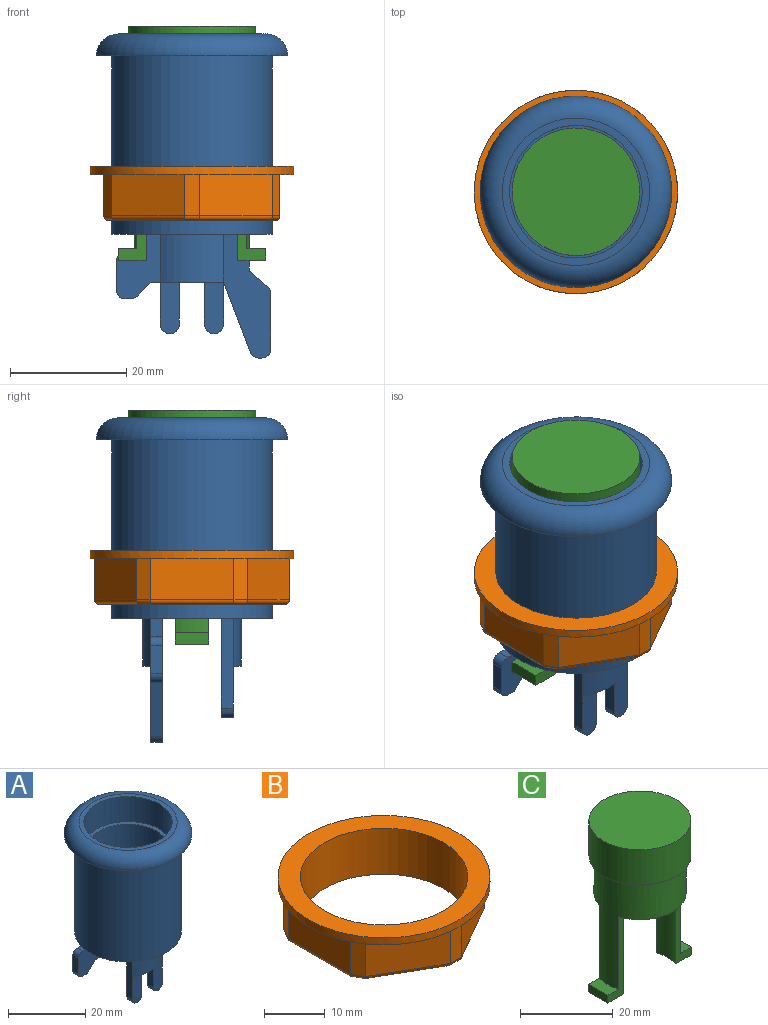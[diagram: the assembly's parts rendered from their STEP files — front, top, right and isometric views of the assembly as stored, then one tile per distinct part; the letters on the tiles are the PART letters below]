
ASSEMBLY  parts=3 mates=2
PART A: 49 faces, bbox 35.7x35.7x55.9 mm
  f0: plane 11.11x7.62mm, normal (0,1,0), area 64.9mm2, adj f1,f29,f30,f31,f37,f38,f39,f42
  f1: plane 27.69x27.69mm, normal (0,0,-1), area 449.5mm2, adj f0,f5,f11,f12,f13,f14,f15,f16
  f2: plane 8.89x3.3mm, normal (0,-1,0), area 28.2mm2, adj f19,f20,f21,f27
  f3: plane 20.57x20.57mm, normal (0,0,1), area 263mm2, adj f10,f11,f12,f13,f14,f15,f16,f17
  f4: plane 25.4x25.4mm, normal (0,0,1), area 96.3mm2, adj f7,f8
  f5: cylinder r=13.84mm len=30.73mm, axis (0,0,1), area 2673.2mm2, adj f1,f6
  f6: plane 33.02x33.02mm, normal (0,0,-1), area 254.3mm2, adj f5,f7
  f7: torus R=12.7mm, axis (0,0,1), area 568.8mm2, adj f4,f6
  f8: cylinder r=11.43mm len=22.86mm, axis (0,0,1), area 570mm2, adj f4,f9
  f9: plane 22.86x22.86mm, normal (0,0,1), area 78mm2, adj f8,f10
  f10: cylinder r=10.29mm len=20.57mm, axis (0,0,1), area 1231.3mm2, adj f3,f9
  f11: plane 7.56x6.48mm, normal (1,0,0), area 48.9mm2, adj f1,f3,f12,f14
  f12: plane 7.56x5mm, normal (0,-1,0), area 37.8mm2, adj f1,f3,f11,f13
  f13: cylinder r=10.03mm len=7.56mm, axis (0,0,-1), area 49.8mm2, adj f1,f3,f12,f14
  f14: plane 7.56x5mm, normal (0,1,0), area 37.8mm2, adj f1,f3,f11,f13
  f15: plane 7.56x6.48mm, normal (-1,0,0), area 48.9mm2, adj f1,f3,f16,f18
  f16: plane 7.56x5mm, normal (0,1,0), area 37.8mm2, adj f1,f3,f15,f17
  f17: cylinder r=10.03mm len=7.56mm, axis (0,0,-1), area 49.8mm2, adj f1,f3,f16,f18
  f18: plane 7.56x5mm, normal (0,-1,0), area 37.8mm2, adj f1,f3,f15,f17
  f19: plane 15.49x2.03mm, normal (-1,0,0), area 31.5mm2, adj f1,f2,f25,f26,f27
  f20: plane 7.24x2.03mm, normal (1,0,0), area 14.7mm2, adj f2,f21,f25,f27
  f21: plane 10.92x3.43mm, normal (0,0,-1), area 19.1mm2, adj f2,f20,f22,f24,f25,f26
  f22: plane 7.24x2.03mm, normal (-1,0,0), area 14.7mm2, adj f21,f24,f25,f28
  f23: plane 15.49x2.03mm, normal (1,0,0), area 31.5mm2, adj f1,f24,f25,f26,f28
  f24: plane 8.89x3.3mm, normal (0,-1,0), area 28.2mm2, adj f21,f22,f23,f28
  f25: plane 17.15x10.92mm, normal (0,1,0), area 146.5mm2, adj f1,f19,f20,f21,f22,f23,f27,f28
  f26: cylinder r=11.37mm len=10.92mm, axis (0,0,1), area 94mm2, adj f1,f19,f21,f23
  f27: cylinder r=1.65mm len=3.3mm, axis (0,1,0), area 10.5mm2, adj f2,f19,f20,f25
  f28: cylinder r=1.65mm len=3.3mm, axis (0,1,0), area 10.5mm2, adj f22,f23,f24,f25
  f29: plane 2.03x1.02mm, normal (0,0,-1), area 2.1mm2, adj f0,f41,f43,f48
  f30: plane 2.41x2.41mm, normal (0.71,0,-0.71), area 6.9mm2, adj f0,f31,f41,f43
  f31: plane 12.51x3.43mm, normal (0,0,-1), area 35.7mm2, adj f0,f30,f32,f41,f42
  f32: plane 12.1x4.63mm, normal (-0.93,0,-0.36), area 26.3mm2, adj f31,f40,f41,f44
  f33: plane 2.03x0.55mm, normal (0,0,-1), area 1.1mm2, adj f40,f41,f44,f45
  f34: plane 9.59x2.03mm, normal (1,0,0), area 19.5mm2, adj f40,f41,f45,f46
  f35: plane 3.15x2.72mm, normal (0.65,0,0.76), area 8.5mm2, adj f36,f40,f41,f46
  f36: plane 6.35x2.03mm, normal (1,0,0), area 12.9mm2, adj f1,f35,f40,f41
  f37: plane 3.18x2.03mm, normal (-1,0,0), area 6.5mm2, adj f0,f1,f38,f41
  f38: plane 2.03x1.65mm, normal (0,0,1), area 3.4mm2, adj f0,f37,f41,f47
  f39: plane 4.89x2.03mm, normal (-1,0,0), area 9.9mm2, adj f0,f41,f47,f48
  f40: plane 21.34x8.13mm, normal (0,1,0), area 110.7mm2, adj f1,f32,f33,f34,f35,f36,f42,f44
  f41: plane 26.67x21.34mm, normal (0,-1,0), area 265.8mm2, adj f1,f29,f30,f31,f32,f33,f34,f35
  f42: cylinder r=11.37mm len=10.92mm, axis (0,0,1), area 94mm2, adj f0,f1,f31,f40
  f43: cylinder r=1.52mm len=2.03mm, axis (0,-1,0), area 2.4mm2, adj f0,f29,f30,f41
  f44: cylinder r=1.52mm len=2.03mm, axis (0,-1,0), area 3.7mm2, adj f32,f33,f40,f41
  f45: cylinder r=1.52mm len=2.03mm, axis (0,-1,0), area 4.9mm2, adj f33,f34,f40,f41
  f46: cylinder r=1.52mm len=2.03mm, axis (0,-1,0), area 2.7mm2, adj f34,f35,f40,f41
  f47: cylinder r=1.52mm len=2.03mm, axis (0,-1,0), area 4.9mm2, adj f0,f38,f39,f41
  f48: cylinder r=1.52mm len=2.03mm, axis (0,-1,0), area 4.9mm2, adj f0,f29,f39,f41
PART B: 29 faces, bbox 35.1x35.1x9.3 mm
  f0: cylinder r=17.53mm len=35.05mm, axis (0,0,1), area 156.6mm2, adj f3,f9
  f1: plane 32x28.83mm, normal (0,0,-1), area 113.6mm2, adj f2,f17,f18,f19,f20,f21,f22,f23
  f2: cylinder r=13.84mm len=27.69mm, axis (0,0,1), area 808.6mm2, adj f1,f3
  f3: plane 35.05x35.05mm, normal (0,0,1), area 363mm2, adj f0,f2
  f4: plane 14.48x7.11mm, normal (-1,0,0), area 103mm2, adj f9,f11,f12,f26
  f5: plane 12.54x7.24mm, normal (0.5,0.87,0), area 103mm2, adj f9,f15,f16,f23
  f6: plane 12.54x7.24mm, normal (0.5,-0.87,0), area 103mm2, adj f9,f13,f14,f18
  f7: plane 14.48x7.11mm, normal (1,0,0), area 103mm2, adj f9,f14,f15,f19
  f8: plane 12.54x7.24mm, normal (-0.5,0.87,0), area 103mm2, adj f9,f11,f16,f27
  f9: plane 35.05x35.05mm, normal (0,0,-1), area 173mm2, adj f0,f4,f5,f6,f7,f8,f10,f11
  f10: plane 12.54x7.24mm, normal (-0.5,-0.87,0), area 103mm2, adj f9,f12,f13,f22
  f11: plane 7.11x2.29mm, normal (-0.87,0.5,0), area 18.8mm2, adj f4,f8,f9,f28
  f12: plane 7.11x2.29mm, normal (-0.87,-0.5,0), area 18.8mm2, adj f4,f9,f10,f24
  f13: plane 7.11x2.64mm, normal (0,-1,0), area 18.8mm2, adj f6,f9,f10,f20
  f14: plane 7.11x2.29mm, normal (0.87,-0.5,0), area 18.8mm2, adj f6,f7,f9,f17
  f15: plane 7.11x2.29mm, normal (0.87,0.5,0), area 18.8mm2, adj f5,f7,f9,f21
  f16: plane 7.11x2.64mm, normal (0,1,0), area 18.8mm2, adj f5,f8,f9,f25
  f17: cylinder r=0.76mm len=2.67mm, axis (0.5,0.87,0), area 3mm2, adj f1,f14,f18,f19
  f18: cylinder r=0.76mm len=12.92mm, axis (-0.87,-0.5,0), area 17.2mm2, adj f1,f6,f17,f20
  f19: cylinder r=0.76mm len=14.48mm, axis (0,-1,0), area 17.2mm2, adj f1,f7,f17,f21
  f20: cylinder r=0.76mm len=2.64mm, axis (1,0,0), area 3mm2, adj f1,f13,f18,f22
  f21: cylinder r=0.76mm len=2.67mm, axis (-0.5,0.87,0), area 3mm2, adj f1,f15,f19,f23
  f22: cylinder r=0.76mm len=12.92mm, axis (-0.87,0.5,0), area 17.2mm2, adj f1,f10,f20,f24
  f23: cylinder r=0.76mm len=12.92mm, axis (0.87,-0.5,0), area 17.2mm2, adj f1,f5,f21,f25
  f24: cylinder r=0.76mm len=2.67mm, axis (0.5,-0.87,0), area 3mm2, adj f1,f12,f22,f26
  f25: cylinder r=0.76mm len=2.64mm, axis (1,0,0), area 3mm2, adj f1,f16,f23,f27
  f26: cylinder r=0.76mm len=14.48mm, axis (0,1,0), area 17.2mm2, adj f1,f4,f24,f28
  f27: cylinder r=0.76mm len=12.92mm, axis (0.87,0.5,0), area 17.2mm2, adj f1,f8,f25,f28
  f28: cylinder r=0.76mm len=2.67mm, axis (0.5,0.87,0), area 3mm2, adj f1,f11,f26,f27
PART C: 18 faces, bbox 25.4x22x40.4 mm
  f0: plane 18.96x7mm, normal (0,0,-1), area 34.5mm2, adj f5,f6,f9,f11
  f1: plane 18.96x7mm, normal (0,0,-1), area 34.5mm2, adj f5,f6,f8,f10
  f2: cylinder r=11mm len=22mm, axis (0,0,-1), area 642.4mm2, adj f3,f4
  f3: plane 22x22mm, normal (0,0,1), area 380mm2, adj f2
  f4: plane 22x22mm, normal (0,0,-1), area 70.9mm2, adj f2,f5
  f5: cylinder r=9.92mm len=29.06mm, axis (0,0,1), area 844.5mm2, adj f0,f1,f4,f8,f9,f10,f11,f12
  f6: cylinder r=8.41mm len=36.42mm, axis (0,0,-1), area 1057.8mm2, adj f0,f1,f7,f8,f9,f10,f11,f14
  f7: plane 16.82x16.82mm, normal (0,0,-1), area 222.1mm2, adj f6
  f8: plane 21.18x4.83mm, normal (0,-1,0), area 40.4mm2, adj f1,f5,f6,f12,f13,f14
  f9: plane 21.18x4.83mm, normal (0,1,0), area 40.4mm2, adj f0,f5,f6,f12,f13,f14
  f10: plane 21.18x4.83mm, normal (0,-1,0), area 40.4mm2, adj f1,f5,f6,f15,f16,f17
  f11: plane 21.18x4.83mm, normal (0,1,0), area 40.4mm2, adj f0,f5,f6,f15,f16,f17
  f12: plane 5.84x3.23mm, normal (0,0,1), area 17.2mm2, adj f5,f8,f9,f13
  f13: plane 5.84x2.03mm, normal (-1,0,0), area 11.9mm2, adj f8,f9,f12,f14
  f14: plane 5.84x4.83mm, normal (0,0,-1), area 26.1mm2, adj f6,f8,f9,f13
  f15: plane 5.84x3.23mm, normal (0,0,1), area 17.2mm2, adj f5,f10,f11,f16
  f16: plane 5.84x2.03mm, normal (1,0,0), area 11.9mm2, adj f10,f11,f15,f17
  f17: plane 5.84x4.83mm, normal (0,0,-1), area 26.1mm2, adj f6,f10,f11,f16
PLACE A t=(-3.91,7.49,-2.65)mm fixed
PLACE B t=(-3.91,7.49,9.04)mm
PLACE C t=(-3.91,7.49,-2.65)mm
MATE fastened C.f2 <-> A.f8  axis (0,0,-1) through (-3.91,7.49,23.96)mm
MATE fastened B.f0 <-> A.f17  axis (0,0,1) through (-3.91,7.49,9.04)mm
